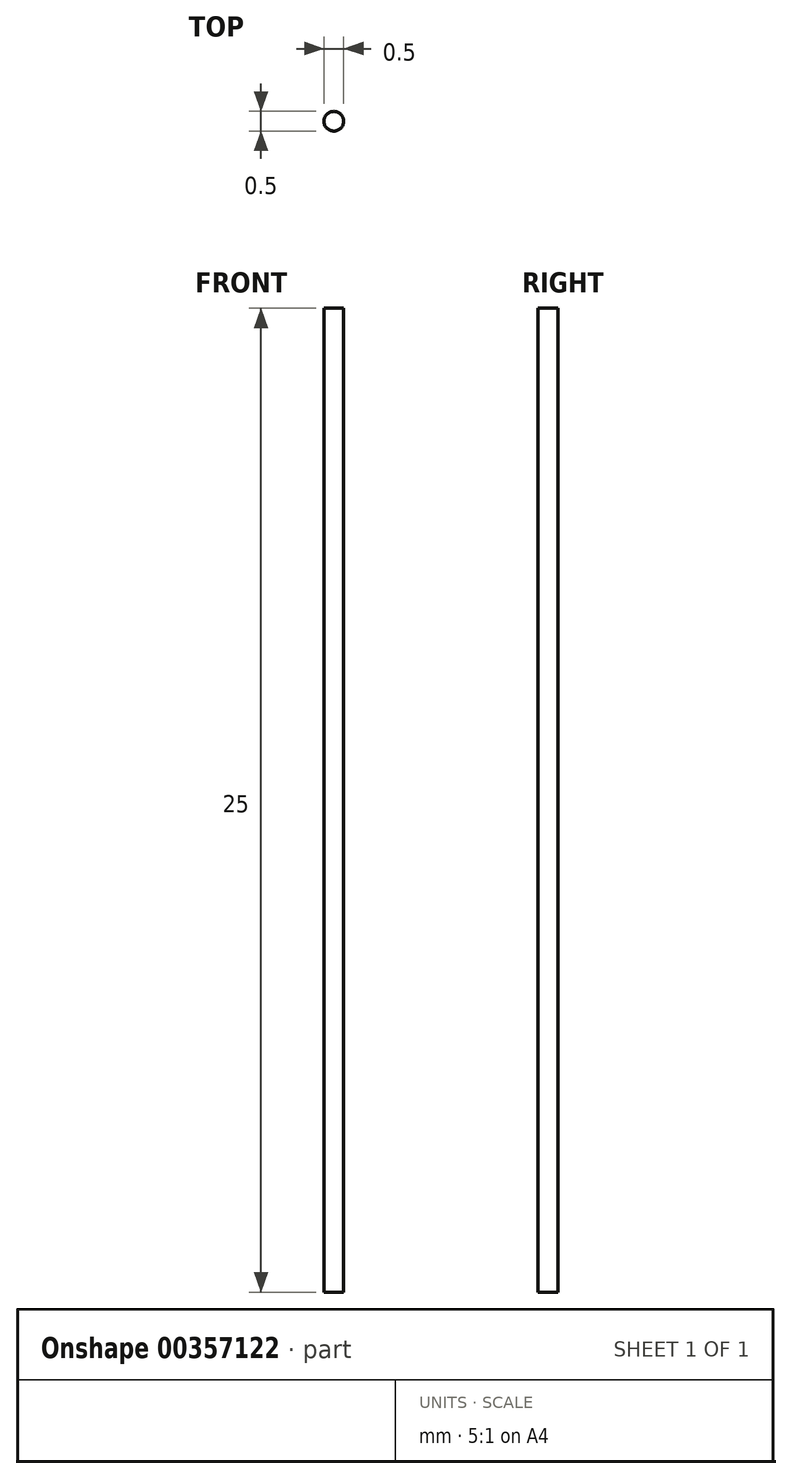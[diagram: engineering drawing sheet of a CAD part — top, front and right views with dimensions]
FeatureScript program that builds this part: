
annotation { "Feature Type Name" : "Feature", "Feature Type Description" : "" }
export const myFeature = defineFeature(function(context is Context, id is Id, definition is map)
    precondition{}
    {
        {
            var Q0;
            Q0=qCreatedBy(makeId("Top.planeOp"),FACE);
            var sketch = newSketch(context, id + "F0", { "sketchPlane" : qUnion([Q0])});
            skCircle(sketch, "E0", {"center": v(0, 0) * mm, "radius": 0.25 * mm});
            skSolve(sketch);
        }
        {
            var Q0;
            Q0=makeQuery(id+"F0.imprint","IMPRINT",FACE,{"disambiguationData":[TD([[makeQuery(id+"F0.imprint","IMPRINT",EDGE,{"derivedFrom":sQuery(id+"F0.wireOp",EDGE,"E0")}),1.0]])]});
            extrude(context, id + "F1", {"entities" : qUnion([Q0]), "depth" : 25 * mm});
        }
    });
